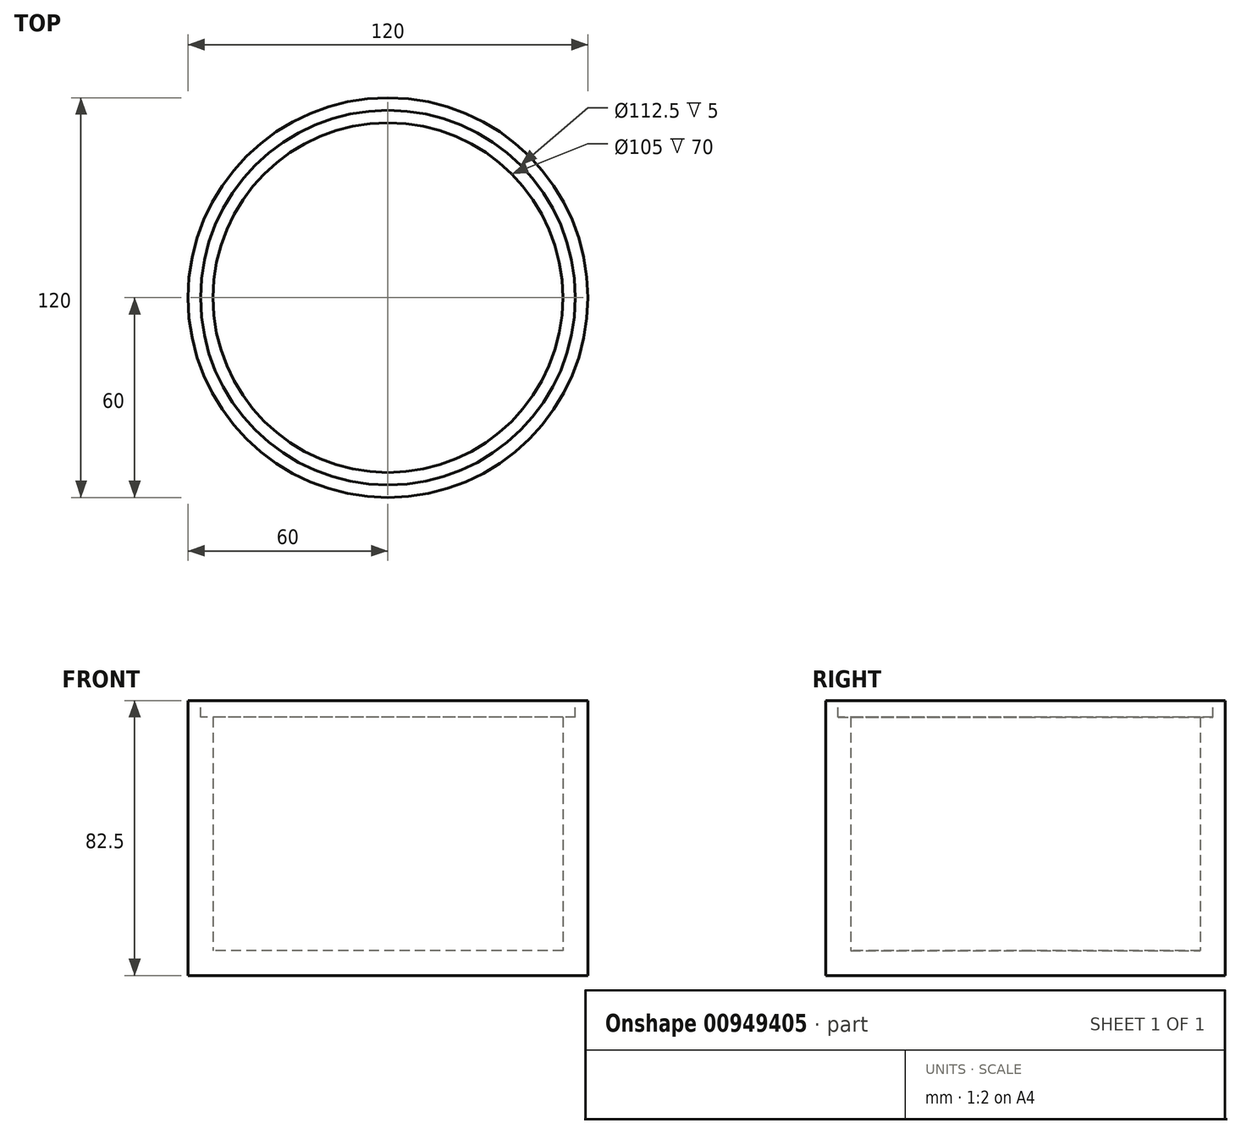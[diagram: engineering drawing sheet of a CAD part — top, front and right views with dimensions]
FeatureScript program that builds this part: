
annotation { "Feature Type Name" : "Feature", "Feature Type Description" : "" }
export const myFeature = defineFeature(function(context is Context, id is Id, definition is map)
    precondition{}
    {
        {
            var Q0;
            Q0=qCreatedBy(makeId("Top.planeOp"),FACE);
            var sketch = newSketch(context, id + "F0", { "sketchPlane" : qUnion([Q0])});
            skCircle(sketch, "E0", {"center": v(0, 0) * mm, "radius": 60 * mm});
            skSolve(sketch);
        }
        {
            var Q0;
            Q0=makeQuery(id+"F0.imprint","IMPRINT",FACE,{"disambiguationData":[TD([[makeQuery(id+"F0.imprint","IMPRINT",EDGE,{"derivedFrom":sQuery(id+"F0.wireOp",EDGE,"E0")}),1.0]])]});
            extrude(context, id + "F1", {"entities" : qUnion([Q0]), "depth" : 7.5 * mm, "offsetDistance" : 25 * mm});
        }
        {
            var Q0;
            Q0=makeQuery(id+"F1.opExtrude","CAP_FACE",FACE,{"disambiguationData":[OSD([sQuery(id+"F0.wireOp",EDGE,"E0")])],"isStart":false});
            var sketch = newSketch(context, id + "F2", { "sketchPlane" : qUnion([Q0])});
            skCircle(sketch, "E1", {"center": v(0, 0) * mm, "radius": 52.5 * mm});
            skSolve(sketch);
        }
        {
            var Q0;
            Q0=makeQuery(id+"F2.imprint","IMPRINT",FACE,{"disambiguationData":[TD([[makeQuery(id+"F2.imprint","IMPRINT",EDGE,{"derivedFrom":sQuery(id+"F2.wireOp",EDGE,"E1")}),-1.0]])]});
            extrude(context, id + "F3", {"entities" : qUnion([Q0]), "operationType" : NewBodyOperationType.ADD, "depth" : 75 * mm, "offsetDistance" : 25 * mm});
        }
        {
            var Q0;
            Q0=makeQuery(id+"F3.opExtrude","CAP_FACE",FACE,{"disambiguationData":[OSD([sQuery(id+"F0.wireOp",EDGE,"E0"),sQuery(id+"F2.wireOp",EDGE,"E1")])],"isStart":false});
            var sketch = newSketch(context, id + "F4", { "sketchPlane" : qUnion([Q0])});
            skCircle(sketch, "E2", {"center": v(0, 0) * mm, "radius": 56.25 * mm});
            skSolve(sketch);
        }
        {
            var Q0;
            Q0=makeQuery(id+"F4.imprint","IMPRINT",FACE,{"disambiguationData":[TD([[makeQuery(id+"F4.imprint","IMPRINT",EDGE,{"derivedFrom":sQuery(id+"F4.wireOp",EDGE,"E2")}),1.0]])]});
            extrude(context, id + "F5", {"entities" : qUnion([Q0]), "operationType" : NewBodyOperationType.REMOVE, "oppositeDirection" : true, "depth" : 5 * mm, "offsetDistance" : 25 * mm});
        }
    });
